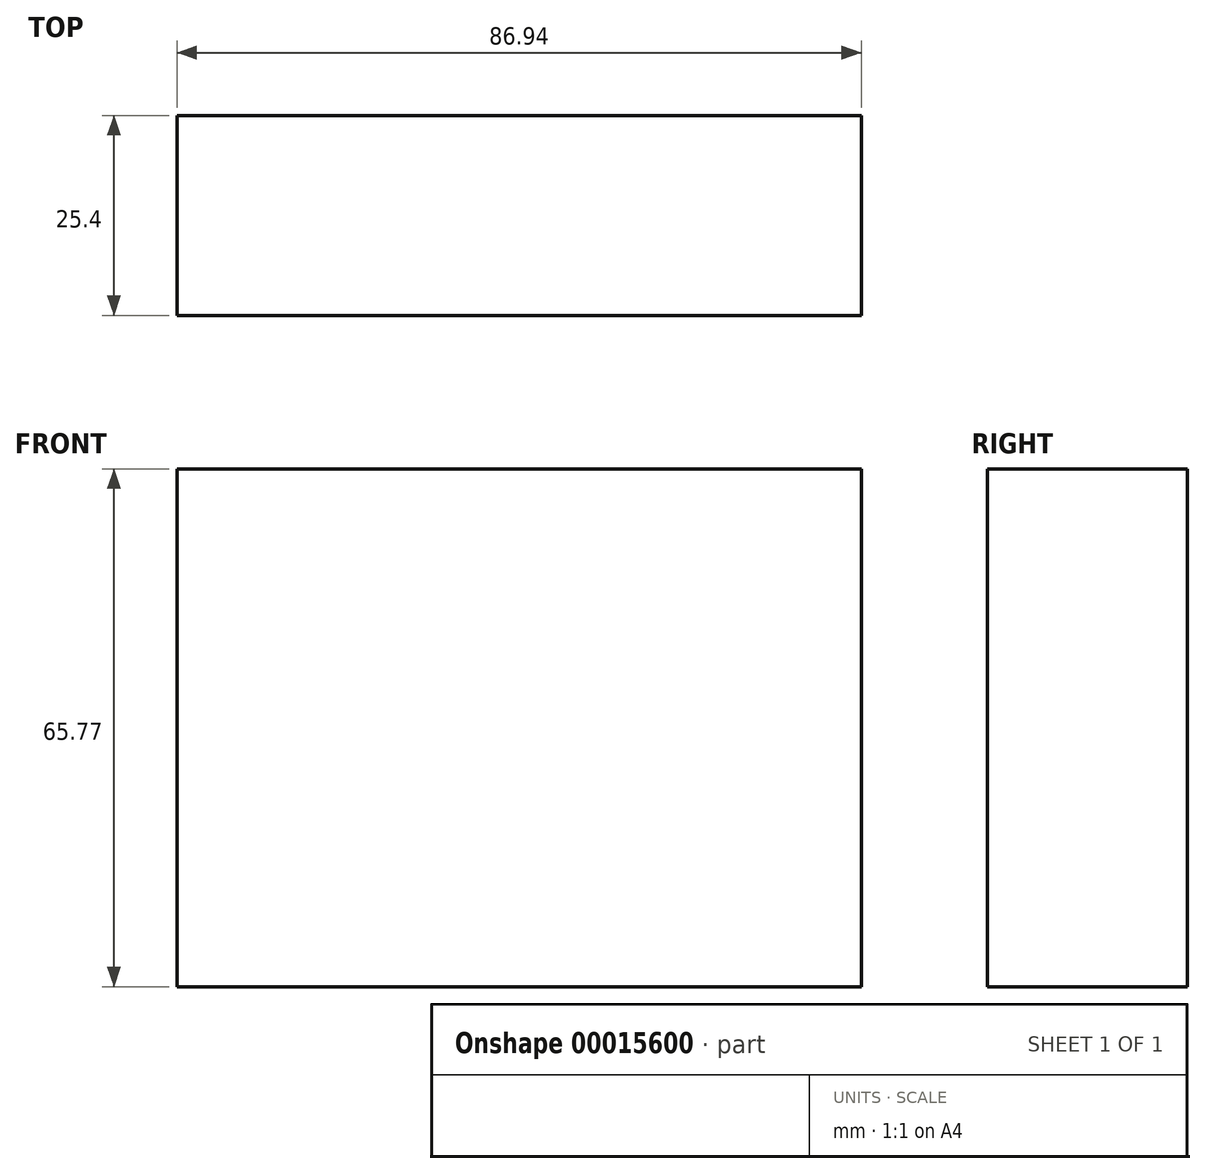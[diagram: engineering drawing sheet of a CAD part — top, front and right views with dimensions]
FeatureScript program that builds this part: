
annotation { "Feature Type Name" : "Feature", "Feature Type Description" : "" }
export const myFeature = defineFeature(function(context is Context, id is Id, definition is map)
    precondition{}
    {
        {
            var Q0;
            Q0=qCreatedBy(makeId("Front.planeOp"),FACE);
            var sketch = newSketch(context, id + "F0", { "sketchPlane" : qUnion([Q0])});
            skLineSegment(sketch, "E0.bottom", {"start": v(-34.52, 32.13) * mm, "end": v(52.42, 32.13) * mm});
            skLineSegment(sketch, "E0.top", {"start": v(-34.52, -33.64) * mm, "end": v(52.42, -33.64) * mm});
            skLineSegment(sketch, "E0.left", {"start": v(-34.52, 32.13) * mm, "end": v(-34.52, -33.64) * mm});
            skLineSegment(sketch, "E0.right", {"start": v(52.42, 32.13) * mm, "end": v(52.42, -33.64) * mm});
            skSolve(sketch);
        }
        {
            var Q0;
            Q0=makeQuery(id+"F0.imprint","IMPRINT",FACE,{"disambiguationData":[TD([[makeQuery(id+"F0.imprint","IMPRINT",EDGE,{"derivedFrom":sQuery(id+"F0.wireOp",EDGE,"E0.bottom")}),-1.0]])]});
            extrude(context, id + "F1", {"entities" : qUnion([Q0]), "depth" : 25.4 * mm});
        }
    });
